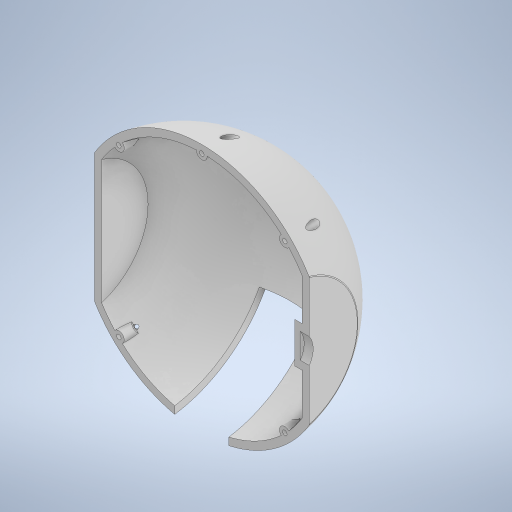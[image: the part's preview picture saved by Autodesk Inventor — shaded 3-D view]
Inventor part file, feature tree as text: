
AUTODESK INVENTOR PART (.ipt)
format: ipt  version: 2023 (Build 270158000, 158)  size: 495,104 bytes
history: native  units: mm
features: sketch x8, extrude x8, other x4, projected_geometry x2, revolve x1, shell x1, fillet x1, chamfer x1
ambient origin geometry x8: Origin, YZ Plane, XZ Plane, XY Plane, X Axis, Y Axis, Z Axis, Center Point
bodies: Body1 (feature_tree)
feature tree (26):
  other  "솔리드1"
  sketch  "스케치1"
  revolve  "회전1"
  other  "작업 평면2"
  extrude  "돌출14"  Depth=85.0mm
  shell  "쉘2"  Thickness=56.0mm
  extrude  "돌출15"  Depth=17.0mm
  other  "작업 평면3"
  fillet  "모깎기3"  Radius=140.0mm
  extrude  "돌출17"  Depth=4.0mm
  sketch  "스케치20"
  extrude  "돌출18"  TaperAngle=360.0deg  [1 undecoded]
  extrude  "돌출19"  [1 undecoded]
  extrude  "돌출20"  Depth=108.0mm TaperAngle=0.0deg
  other  "작업 평면4"
  sketch  "스케치24"
  chamfer  "모따기2"  Distance=4.0mm
  extrude  "돌출23"  Depth=2.5mm
  extrude  "돌출24"  Depth=80.0mm TaperAngle=360.0deg
  sketch  "스케치16"
  sketch  "스케치17"
  projected_geometry  "투영된 루프4"
  sketch  "스케치19"
  sketch  "스케치21"
  sketch  "스케치22"
  projected_geometry  "투영된 루프5"
note: 2 required parameter values undecoded (feature->parameter linkage not recoverable at this tier; creation-order binding heuristic only, values carry confidence <= 0.55)
